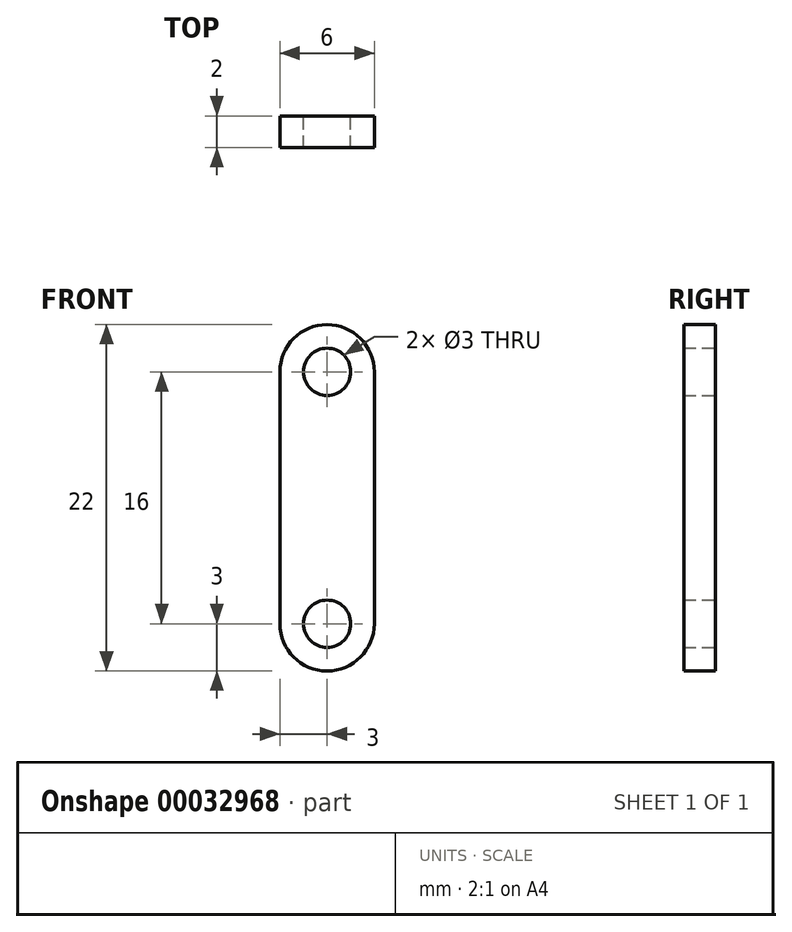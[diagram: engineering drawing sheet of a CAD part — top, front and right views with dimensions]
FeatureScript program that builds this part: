
annotation { "Feature Type Name" : "Feature", "Feature Type Description" : "" }
export const myFeature = defineFeature(function(context is Context, id is Id, definition is map)
    precondition{}
    {
        {
            var Q0;
            Q0=qCreatedBy(makeId("Front.planeOp"),FACE);
            var sketch = newSketch(context, id + "F0", { "sketchPlane" : qUnion([Q0])});
            skLineSegment(sketch, "E0.rect.left", {"start": v(3, -25) * mm, "end": v(3, -9) * mm});
            skLineSegment(sketch, "E0.rect.right", {"start": v(-3, -25) * mm, "end": v(-3, -9) * mm});
            skPoint(sketch, "E0.rect.middle", {"position": v(0, 0) * mm});
            skArc(sketch, "E1.MirrorCS", {"start": v(3, -25) * mm, "mid": v(0, -28) * mm, "end": v(-3, -25) * mm});
            skCircle(sketch, "E2.MirrorC", {"center": v(0, -25) * mm, "radius": 1.5 * mm});
            skCircle(sketch, "E3", {"center": v(0, -9) * mm, "radius": 1.5 * mm});
            skArc(sketch, "E4", {"start": v(3, -9) * mm, "mid": v(0, -6) * mm, "end": v(-3, -9) * mm});
            skSolve(sketch);
        }
        {
            var Q0;
            Q0=qSketchRegion(id+"F0",true);
            extrude(context, id + "F1", {"entities" : qUnion([Q0]), "depth" : 2 * mm});
        }
    });
